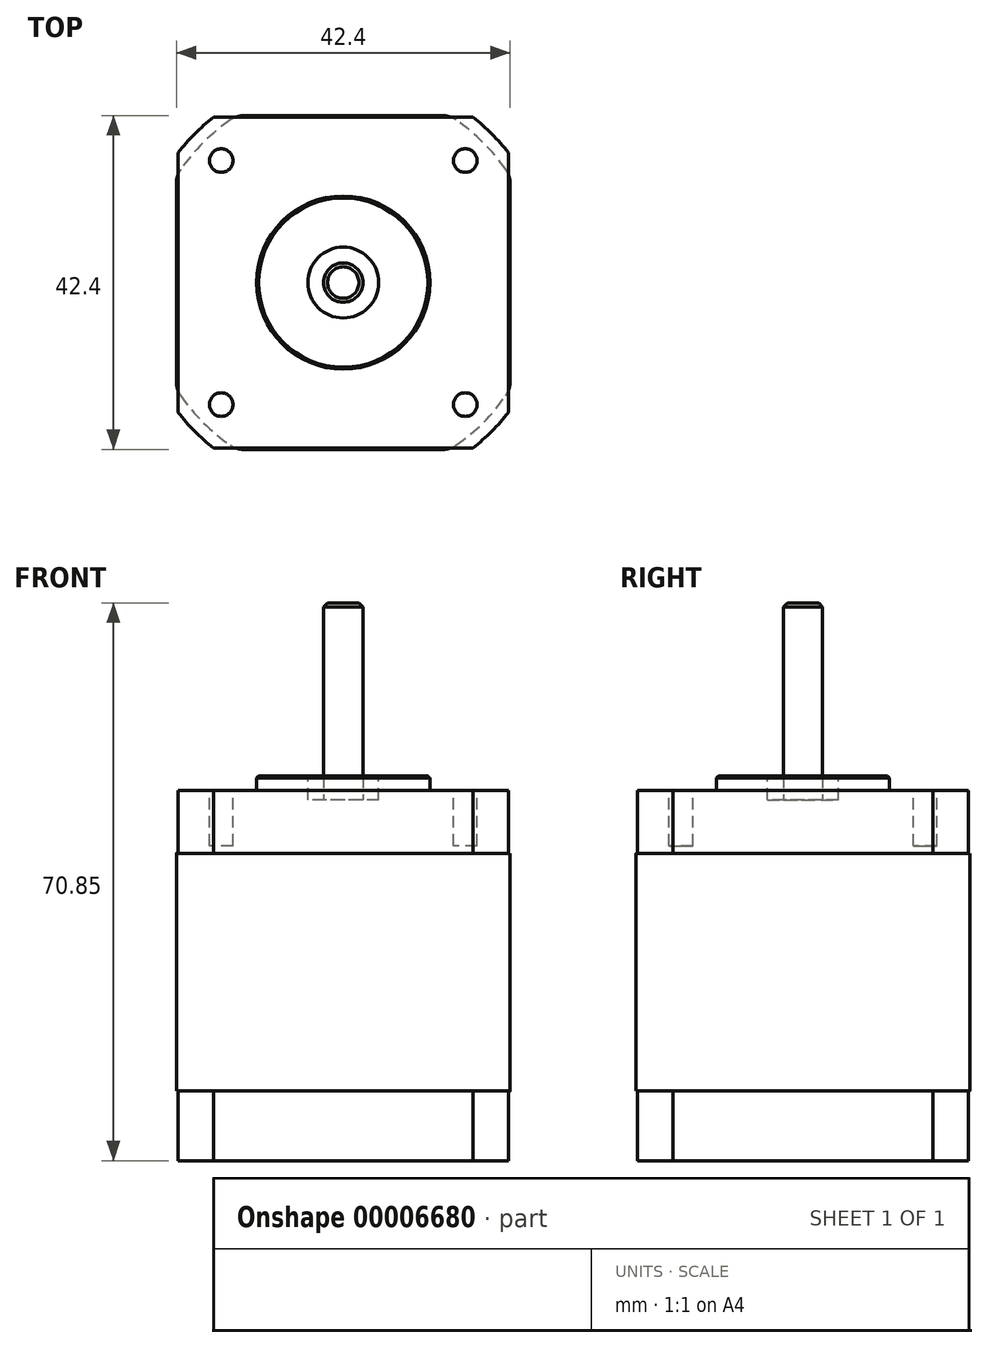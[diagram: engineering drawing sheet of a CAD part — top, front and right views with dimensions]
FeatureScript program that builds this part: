
annotation { "Feature Type Name" : "Feature", "Feature Type Description" : "" }
export const myFeature = defineFeature(function(context is Context, id is Id, definition is map)
    precondition{}
    {
        {
            var Q0;
            Q0=qCreatedBy(makeId("Top.planeOp"),FACE);
            var sketch = newSketch(context, id + "F0", { "sketchPlane" : qUnion([Q0])});
            skLineSegment(sketch, "E0.bottom", {"start": v(4.51, 0) * mm, "end": v(37.49, 0) * mm});
            skLineSegment(sketch, "E0.top", {"start": v(4.51, 42) * mm, "end": v(37.49, 42) * mm});
            skLineSegment(sketch, "E0.left", {"start": v(0, 4.51) * mm, "end": v(0, 37.49) * mm});
            skLineSegment(sketch, "E0.right", {"start": v(42, 4.51) * mm, "end": v(42, 37.49) * mm});
            skArc(sketch, "E1", {"start": v(4.51, 42) * mm, "mid": v(2.12, 39.88) * mm, "end": v(0, 37.49) * mm});
            skArc(sketch, "E2.trimOffspring", {"start": v(42, 37.49) * mm, "mid": v(39.88, 39.88) * mm, "end": v(37.49, 42) * mm});
            skArc(sketch, "E3.trimOffspring", {"start": v(37.49, 0) * mm, "mid": v(39.88, 2.12) * mm, "end": v(42, 4.51) * mm});
            skArc(sketch, "E4.trimOffspring", {"start": v(0, 4.51) * mm, "mid": v(2.12, 2.12) * mm, "end": v(4.51, 0) * mm});
            skSolve(sketch);
        }
        {
            var Q0;
            Q0 = qSketchRegion(id + "F0", true);
            extrude(context, id + "F1", {"entities" : qUnion([Q0]), "depth" : 8.85 * mm});
        }
        {
            var Q0;
            Q0=makeQuery(id+"F1.opExtrude","CAP_FACE",FACE,{"disambiguationData":[OSD([sQuery(id+"F0.wireOp",EDGE,"E0.bottom"),sQuery(id+"F0.wireOp",EDGE,"E0.top"),sQuery(id+"F0.wireOp",EDGE,"E0.left"),sQuery(id+"F0.wireOp",EDGE,"E0.right"),sQuery(id+"F0.wireOp",EDGE,"E1"),sQuery(id+"F0.wireOp",EDGE,"E2.trimOffspring"),sQuery(id+"F0.wireOp",EDGE,"E3.trimOffspring"),sQuery(id+"F0.wireOp",EDGE,"E4.trimOffspring")])],"isStart":false});
            var sketch = newSketch(context, id + "F2", { "sketchPlane" : qUnion([Q0])});
            skLineSegment(sketch, "E5.bottom", {"start": v(8.38, 42.2) * mm, "end": v(33.62, 42.2) * mm});
            skLineSegment(sketch, "E5.top", {"start": v(8.38, -0.2) * mm, "end": v(33.62, -0.2) * mm});
            skLineSegment(sketch, "E5.left", {"start": v(-0.2, 33.62) * mm, "end": v(-0.2, 8.38) * mm});
            skLineSegment(sketch, "E5.right", {"start": v(42.2, 33.62) * mm, "end": v(42.2, 8.38) * mm});
            skArc(sketch, "E6", {"start": v(0.33, 6.67) * mm, "mid": v(3.22, 3.22) * mm, "end": v(6.67, 0.33) * mm});
            skArc(sketch, "E7.trimOffspring", {"start": v(35.33, 0.33) * mm, "mid": v(38.78, 3.22) * mm, "end": v(41.67, 6.67) * mm});
            skArc(sketch, "E8.trimOffspring", {"start": v(41.67, 35.33) * mm, "mid": v(38.78, 38.78) * mm, "end": v(35.33, 41.67) * mm});
            skArc(sketch, "E9.trimOffspring", {"start": v(6.67, 41.67) * mm, "mid": v(3.22, 38.78) * mm, "end": v(0.33, 35.33) * mm});
            skPoint(sketch, "E10.visualSharp", {"position": v(7.47, 42.2) * mm});
            skArc(sketch, "E10.filletArc", {"start": v(8.38, 42.2) * mm, "mid": v(7.48, 42.06) * mm, "end": v(6.67, 41.67) * mm});
            skPoint(sketch, "E11.visualSharp", {"position": v(-0.2, 34.53) * mm});
            skArc(sketch, "E11.filletArc", {"start": v(0.33, 35.33) * mm, "mid": v(-0.06, 34.52) * mm, "end": v(-0.2, 33.62) * mm});
            skPoint(sketch, "E12.visualSharp", {"position": v(-0.2, 7.47) * mm});
            skArc(sketch, "E12.filletArc", {"start": v(-0.2, 8.38) * mm, "mid": v(-0.06, 7.48) * mm, "end": v(0.33, 6.67) * mm});
            skPoint(sketch, "E13.visualSharp", {"position": v(7.47, -0.2) * mm});
            skArc(sketch, "E13.filletArc", {"start": v(6.67, 0.33) * mm, "mid": v(7.48, -0.06) * mm, "end": v(8.38, -0.2) * mm});
            skPoint(sketch, "E14.visualSharp", {"position": v(34.53, -0.2) * mm});
            skArc(sketch, "E14.filletArc", {"start": v(33.62, -0.2) * mm, "mid": v(34.52, -0.06) * mm, "end": v(35.33, 0.33) * mm});
            skPoint(sketch, "E15.visualSharp", {"position": v(42.2, 7.47) * mm});
            skArc(sketch, "E15.filletArc", {"start": v(41.67, 6.67) * mm, "mid": v(42.06, 7.48) * mm, "end": v(42.2, 8.38) * mm});
            skPoint(sketch, "E16.visualSharp", {"position": v(42.2, 34.53) * mm});
            skArc(sketch, "E16.filletArc", {"start": v(42.2, 33.62) * mm, "mid": v(42.06, 34.52) * mm, "end": v(41.67, 35.33) * mm});
            skPoint(sketch, "E17.visualSharp", {"position": v(34.53, 42.2) * mm});
            skArc(sketch, "E17.filletArc", {"start": v(35.33, 41.67) * mm, "mid": v(34.52, 42.06) * mm, "end": v(33.62, 42.2) * mm});
            skSolve(sketch);
        }
        {
            var Q0;
            Q0 = qSketchRegion(id + "F2", true);
            extrude(context, id + "F3", {"entities" : qUnion([Q0]), "depth" : 30.2 * mm});
        }
        {
            var Q0;
            Q0=makeQuery(id+"F3.opExtrude","CAP_FACE",FACE,{"disambiguationData":[OSD([sQuery(id+"F2.wireOp",EDGE,"E5.bottom"),sQuery(id+"F2.wireOp",EDGE,"E5.top"),sQuery(id+"F2.wireOp",EDGE,"E5.left"),sQuery(id+"F2.wireOp",EDGE,"E5.right"),sQuery(id+"F2.wireOp",EDGE,"E6"),sQuery(id+"F2.wireOp",EDGE,"E7.trimOffspring"),sQuery(id+"F2.wireOp",EDGE,"E8.trimOffspring"),sQuery(id+"F2.wireOp",EDGE,"E9.trimOffspring"),sQuery(id+"F2.wireOp",EDGE,"E10.filletArc"),sQuery(id+"F2.wireOp",EDGE,"E11.filletArc"),sQuery(id+"F2.wireOp",EDGE,"E12.filletArc"),sQuery(id+"F2.wireOp",EDGE,"E13.filletArc"),sQuery(id+"F2.wireOp",EDGE,"E14.filletArc"),sQuery(id+"F2.wireOp",EDGE,"E15.filletArc"),sQuery(id+"F2.wireOp",EDGE,"E16.filletArc"),sQuery(id+"F2.wireOp",EDGE,"E17.filletArc")])],"isStart":false});
            var sketch = newSketch(context, id + "F4", { "sketchPlane" : qUnion([Q0])});
            skLineSegment(sketch, "E18.bottom", {"start": v(4.51, 0) * mm, "end": v(37.49, 0) * mm});
            skLineSegment(sketch, "E18.top", {"start": v(4.51, 42) * mm, "end": v(37.49, 42) * mm});
            skLineSegment(sketch, "E18.left", {"start": v(0, 4.51) * mm, "end": v(0, 37.49) * mm});
            skLineSegment(sketch, "E18.right", {"start": v(42, 4.51) * mm, "end": v(42, 37.49) * mm});
            skArc(sketch, "E19", {"start": v(0, 4.51) * mm, "mid": v(2.12, 2.12) * mm, "end": v(4.51, 0) * mm});
            skArc(sketch, "E20.trimOffspring", {"start": v(4.51, 42) * mm, "mid": v(2.12, 39.88) * mm, "end": v(0, 37.49) * mm});
            skArc(sketch, "E21.trimOffspring", {"start": v(42, 37.49) * mm, "mid": v(39.88, 39.88) * mm, "end": v(37.49, 42) * mm});
            skArc(sketch, "E22.trimOffspring", {"start": v(37.49, 0) * mm, "mid": v(39.88, 2.12) * mm, "end": v(42, 4.51) * mm});
            skSolve(sketch);
        }
        {
            var Q0;
            Q0 = qSketchRegion(id + "F4", true);
            extrude(context, id + "F5", {"entities" : qUnion([Q0]), "depth" : 7.95 * mm});
        }
        {
            var Q0;
            Q0=makeQuery(id+"F5.opExtrude","CAP_FACE",FACE,{"disambiguationData":[OSD([sQuery(id+"F4.wireOp",EDGE,"E18.bottom"),sQuery(id+"F4.wireOp",EDGE,"E18.top"),sQuery(id+"F4.wireOp",EDGE,"E18.left"),sQuery(id+"F4.wireOp",EDGE,"E18.right"),sQuery(id+"F4.wireOp",EDGE,"E19"),sQuery(id+"F4.wireOp",EDGE,"E20.trimOffspring"),sQuery(id+"F4.wireOp",EDGE,"E21.trimOffspring"),sQuery(id+"F4.wireOp",EDGE,"E22.trimOffspring")])],"isStart":false});
            var sketch = newSketch(context, id + "F6", { "sketchPlane" : qUnion([Q0])});
            skCircle(sketch, "E23", {"center": v(21, 21) * mm, "radius": 11 * mm});
            skSolve(sketch);
        }
        {
            var Q0;
            Q0 = qSketchRegion(id + "F6", true);
            extrude(context, id + "F7", {"entities" : qUnion([Q0]), "operationType" : NewBodyOperationType.ADD, "depth" : 1.85 * mm});
        }
        {
            var Q0;
            Q0=makeQuery(id+"F7.opExtrude","CAP_FACE",FACE,{"disambiguationData":[OSD([sQuery(id+"F6.wireOp",EDGE,"E23")])],"isStart":false});
            var sketch = newSketch(context, id + "F8", { "sketchPlane" : qUnion([Q0])});
            skCircle(sketch, "E24", {"center": v(21, 21) * mm, "radius": 4.5 * mm});
            skSolve(sketch);
        }
        {
            var Q0;
            Q0 = qSketchRegion(id + "F8", true);
            extrude(context, id + "F9", {"entities" : qUnion([Q0]), "operationType" : NewBodyOperationType.REMOVE, "oppositeDirection" : true, "depth" : 3 * mm});
        }
        {
            var Q0;
            Q0=makeQuery(id+"F9.boolean.opBoolean","COPY",FACE,{"derivedFrom":makeQuery(id+"F9.opExtrude","CAP_FACE",FACE,{"disambiguationData":[OSD([sQuery(id+"F8.wireOp",EDGE,"E24")])],"isStart":false})});
            var sketch = newSketch(context, id + "F10", { "sketchPlane" : qUnion([Q0])});
            skCircle(sketch, "E25", {"center": v(21, 21) * mm, "radius": 2.5 * mm});
            skSolve(sketch);
        }
        {
            var Q0;
            Q0 = qSketchRegion(id + "F10", true);
            extrude(context, id + "F11", {"entities" : qUnion([Q0]), "depth" : 25 * mm});
        }
        {
            var Q0;
            Q0=makeQuery(id+"F11.opExtrude","CAP_EDGE",EDGE,{"disambiguationData":[OSD([sQuery(id+"F10.wireOp",EDGE,"E25")])],"isStart":false});
            chamfer(context, id + "F12", {"entities" : qUnion([Q0]), "width" : 0.5 * mm, "tangentPropagation" : true});
        }
        {
            var Q0;
            Q0=makeQuery(id+"F5.opExtrude","CAP_FACE",FACE,{"disambiguationData":[OSD([sQuery(id+"F4.wireOp",EDGE,"E18.bottom"),sQuery(id+"F4.wireOp",EDGE,"E18.top"),sQuery(id+"F4.wireOp",EDGE,"E18.left"),sQuery(id+"F4.wireOp",EDGE,"E18.right"),sQuery(id+"F4.wireOp",EDGE,"E19"),sQuery(id+"F4.wireOp",EDGE,"E20.trimOffspring"),sQuery(id+"F4.wireOp",EDGE,"E21.trimOffspring"),sQuery(id+"F4.wireOp",EDGE,"E22.trimOffspring")])],"isStart":false});
            var sketch = newSketch(context, id + "F13", { "sketchPlane" : qUnion([Q0])});
            skCircle(sketch, "E26", {"center": v(5.5, 36.5) * mm, "radius": 1.5 * mm});
            skCircle(sketch, "E27", {"center": v(36.5, 36.5) * mm, "radius": 1.5 * mm});
            skCircle(sketch, "E28", {"center": v(36.5, 5.5) * mm, "radius": 1.5 * mm});
            skCircle(sketch, "E29", {"center": v(5.5, 5.5) * mm, "radius": 1.5 * mm});
            skSolve(sketch);
        }
        {
            var Q0;
            Q0 = qSketchRegion(id + "F13", true);
            extrude(context, id + "F14", {"entities" : qUnion([Q0]), "operationType" : NewBodyOperationType.REMOVE, "oppositeDirection" : true, "depth" : 7 * mm});
        }
        {
            var Q0;
            Q0=makeQuery(id+"F14.boolean.opBoolean","COPY",EDGE,{"derivedFrom":makeQuery(id+"F14.opExtrude","CAP_EDGE",EDGE,{"disambiguationData":[OSD([sQuery(id+"F13.wireOp",EDGE,"E26")])],"isStart":true})});
            var Q1;
            Q1=makeQuery(id+"F14.boolean.opBoolean","COPY",EDGE,{"derivedFrom":makeQuery(id+"F14.opExtrude","CAP_EDGE",EDGE,{"disambiguationData":[OSD([sQuery(id+"F13.wireOp",EDGE,"E27")])],"isStart":true})});
            var Q2;
            Q2=makeQuery(id+"F14.boolean.opBoolean","COPY",EDGE,{"derivedFrom":makeQuery(id+"F14.opExtrude","CAP_EDGE",EDGE,{"disambiguationData":[OSD([sQuery(id+"F13.wireOp",EDGE,"E28")])],"isStart":true})});
            var Q3;
            Q3=makeQuery(id+"F14.boolean.opBoolean","COPY",EDGE,{"derivedFrom":makeQuery(id+"F14.opExtrude","CAP_EDGE",EDGE,{"disambiguationData":[OSD([sQuery(id+"F13.wireOp",EDGE,"E29")])],"isStart":true})});
            var Q4;
            Q4=makeQuery(id+"F7.opExtrude","CAP_EDGE",EDGE,{"disambiguationData":[OSD([sQuery(id+"F6.wireOp",EDGE,"E23")])],"isStart":false});
            var Q5;
            Q5=makeQuery(id+"F9.boolean.opBoolean","COPY",EDGE,{"derivedFrom":makeQuery(id+"F9.opExtrude","CAP_EDGE",EDGE,{"disambiguationData":[OSD([sQuery(id+"F8.wireOp",EDGE,"E24")])],"isStart":true})});
            chamfer(context, id + "F15", {"entities" : qUnion([Q0, Q1, Q2, Q3, Q4, Q5]), "width" : 0.25 * mm, "tangentPropagation" : true});
        }
    });
